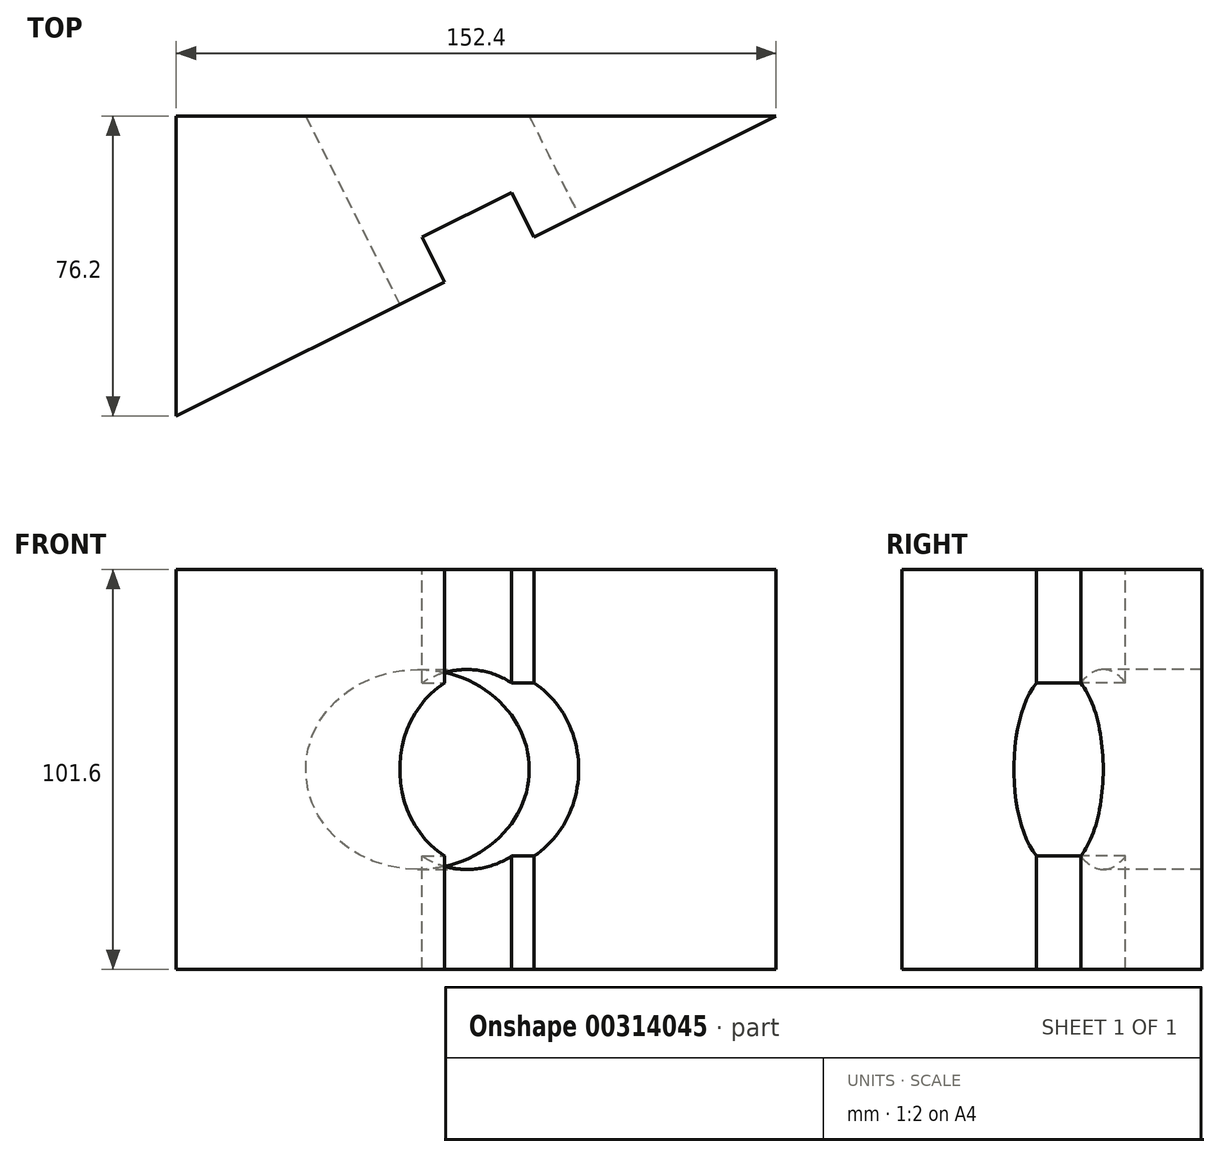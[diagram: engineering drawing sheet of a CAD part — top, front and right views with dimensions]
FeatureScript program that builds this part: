
annotation { "Feature Type Name" : "Feature", "Feature Type Description" : "" }
export const myFeature = defineFeature(function(context is Context, id is Id, definition is map)
    precondition{}
    {
        {
            var Q0;
            Q0=qCreatedBy(makeId("Top.planeOp"),FACE);
            var sketch = newSketch(context, id + "F0", { "sketchPlane" : qUnion([Q0])});
            skLineSegment(sketch, "E0.bottom", {"start": v(0, 0) * mm, "end": v(152.4, 0) * mm});
            skLineSegment(sketch, "E0.top", {"start": v(0, -76.2) * mm, "end": v(152.4, -76.2) * mm});
            skLineSegment(sketch, "E0.left", {"start": v(0, 0) * mm, "end": v(0, -76.2) * mm});
            skLineSegment(sketch, "E0.right", {"start": v(152.4, 0) * mm, "end": v(152.4, -76.2) * mm});
            skLineSegment(sketch, "E1", {"start": v(0, -76.2) * mm, "end": v(152.4, 0) * mm});
            skSolve(sketch);
        }
        {
            var Q0;
            Q0=makeQuery(id+"F0.imprint","IMPRINT",FACE,{"disambiguationData":[TD([[makeQuery(id+"F0.imprint","IMPRINT",EDGE,{"derivedFrom":sQuery(id+"F0.wireOp",EDGE,"E0.bottom")}),-1.0]])]});
            extrude(context, id + "F1", {"entities" : qUnion([Q0]), "depth" : 101.6 * mm});
        }
        {
            var Q0;
            Q0=makeQuery(id+"F1.opExtrude","SWEPT_FACE",FACE,{"disambiguationData":[OSD([sQuery(id+"F0.wireOp",EDGE,"E1")])]});
            var sketch = newSketch(context, id + "F2", { "sketchPlane" : qUnion([Q0])});
            skLineSegment(sketch, "E2.bottom", {"start": v(42.12, 0) * mm, "end": v(67.52, 0) * mm});
            skLineSegment(sketch, "E2.top", {"start": v(42.12, 101.6) * mm, "end": v(67.52, 101.6) * mm});
            skLineSegment(sketch, "E2.left", {"start": v(42.12, 0) * mm, "end": v(42.12, 101.6) * mm});
            skLineSegment(sketch, "E2.right", {"start": v(67.52, 0) * mm, "end": v(67.52, 101.6) * mm});
            skPoint(sketch, "E2.middle", {"position": v(54.82, 50.8) * mm});
            skSolve(sketch);
        }
        {
            var Q0;
            Q0=makeQuery(id+"F2.imprint","IMPRINT",FACE,{"disambiguationData":[TD([[makeQuery(id+"F2.imprint","IMPRINT",EDGE,{"derivedFrom":sQuery(id+"F2.wireOp",EDGE,"E2.bottom")}),1.0]])]});
            extrude(context, id + "F3", {"entities" : qUnion([Q0]), "operationType" : NewBodyOperationType.REMOVE, "oppositeDirection" : true, "depth" : 12.7 * mm});
        }
        {
            var Q0;
            {var subQ0=sQuery(id+"F0.wireOp",EDGE,"E0.bottom");var subQ1=sQuery(id+"F0.wireOp",EDGE,"E1");Q0=makeQuery(id+"F3.boolean.opBoolean","SPLIT",FACE,{"disambiguationData":[TD([makeQuery(id+"F1.opExtrude","SWEPT_FACE",FACE,{"disambiguationData":[OSD([subQ0])]})])],"derivedFrom":makeQuery(id+"F1.opExtrude","SWEPT_FACE",FACE,{"disambiguationData":[OSD([subQ1])]})});}
            var sketch = newSketch(context, id + "F4", { "sketchPlane" : qUnion([Q0])});
            skCircle(sketch, "E3", {"center": v(54.82, 50.8) * mm, "radius": 25.4 * mm});
            skSolve(sketch);
        }
        {
            var Q0;
            {var subQ0=sQuery(id+"F4.wireOp",EDGE,"E3");var subQ1=makeQuery(id+"F3.boolean.opBoolean","COPY",EDGE,{"derivedFrom":makeQuery(id+"F3.opExtrude","CAP_EDGE",EDGE,{"disambiguationData":[OSD([sQuery(id+"F2.wireOp",EDGE,"E2.right")])],"isStart":true})});var subQ2=makeQuery(id+"F4.imprint","INTERSECT",VERTEX,{"disambiguationData":[OD(0.0)],"derivedFrom":[subQ1,subQ0]});Q0=makeQuery(id+"F4.imprint","IMPRINT",FACE,{"disambiguationData":[TD([[makeQuery(id+"F4.imprint","IMPRINT",EDGE,{"disambiguationData":[TD([[subQ2,-1.0]])],"derivedFrom":subQ0}),1.0]])]});}
            var Q1;
            {var subQ0=sQuery(id+"F4.wireOp",EDGE,"E3");var subQ1=makeQuery(id+"F3.boolean.opBoolean","COPY",EDGE,{"derivedFrom":makeQuery(id+"F3.opExtrude","CAP_EDGE",EDGE,{"disambiguationData":[OSD([sQuery(id+"F2.wireOp",EDGE,"E2.right")])],"isStart":true})});var subQ2=makeQuery(id+"F4.imprint","INTERSECT",VERTEX,{"disambiguationData":[OD(0.0)],"derivedFrom":[subQ1,subQ0]});Q1=makeQuery(id+"F4.imprint","IMPRINT",FACE,{"disambiguationData":[TD([[makeQuery(id+"F4.imprint","IMPRINT",EDGE,{"disambiguationData":[TD([[subQ2,1.0]])],"derivedFrom":subQ0}),1.0]])]});}
            extrude(context, id + "F5", {"entities" : qUnion([Q0, Q1]), "operationType" : NewBodyOperationType.REMOVE, "endBound" : BoundingType.THROUGH_ALL, "oppositeDirection" : true, "depth" : 25.4 * mm});
        }
    });
